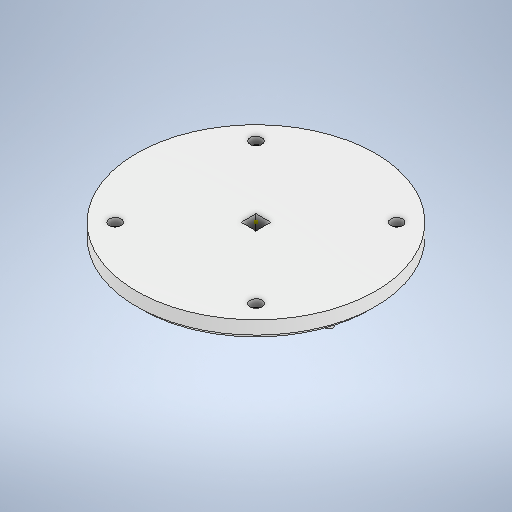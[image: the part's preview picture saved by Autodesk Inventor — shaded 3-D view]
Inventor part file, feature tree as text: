
AUTODESK INVENTOR PART (.ipt)
format: ipt  version: 2025.2 (Build 292293000, 293)  size: 333,824 bytes
history: native  units: mm
features: sketch x7, extrude x3, pattern_circular x2, revolve x1, rib x1, hole x1, chamfer x1
ambient origin geometry x8: Origin, YZ Plane, XZ Plane, XY Plane, X Axis, Y Axis, Z Axis, Center Point
bodies: Solid1 (feature_tree)
feature tree (16):
  revolve  "Revolution1"  [1 undecoded]
  extrude  "Extrusion1"  TaperAngle=360.0deg  [1 undecoded]
  sketch  "Sketch3"  dims[d7=5.6mm]
  rib  "Rib1"
  pattern_circular  "Circular Pattern1"  Count=6 Angle=360.0deg
  sketch  "Sketch5"  dims[d11=15.0mm]
  extrude  "Extrusion2"  Depth=10.0mm
  sketch  "Sketch6"  dims[d12=3.0mm d13=3.0mm d14=0.0mm d15=0.0mm d16=1.0mm d17=1.0mm d18=60.0mm d19=360.0deg]
  extrude  "Extrusion3"  TaperAngle=0.0deg  [1 undecoded]
  hole  "Hole1"  [1 undecoded]
  pattern_circular  "Circular Pattern2"  Count=4 Angle=360.0deg
  chamfer  "Chamfer1"  Distance=37.5mm
  sketch  "Sketch1"  dims[d2=17.5mm d3=45.0mm]
  sketch  "Sketch2"  dims[d4=22.0mm d5=360.0deg]
  sketch  "Sketch4"  dims[d8=10.0mm d9=0.0mm]
  sketch  "Sketch7"  dims[d21=3.0mm d22=10.0mm d23=0.0mm d24=0.0mm d25=2.0mm d26=0.0mm d30=40.0mm d31=360.0deg d34=37.5mm d35=4.5mm d36=6.0mm d37=7.5mm d38=4.2mm d39=90.0deg d40=8.0mm d41=20.594885mm d42=45.0deg d43=2.0mm d44=2.0mm d45=45.0deg]
note: 4 required parameter values undecoded (feature->parameter linkage not recoverable at this tier; creation-order binding heuristic only, values carry confidence <= 0.55)